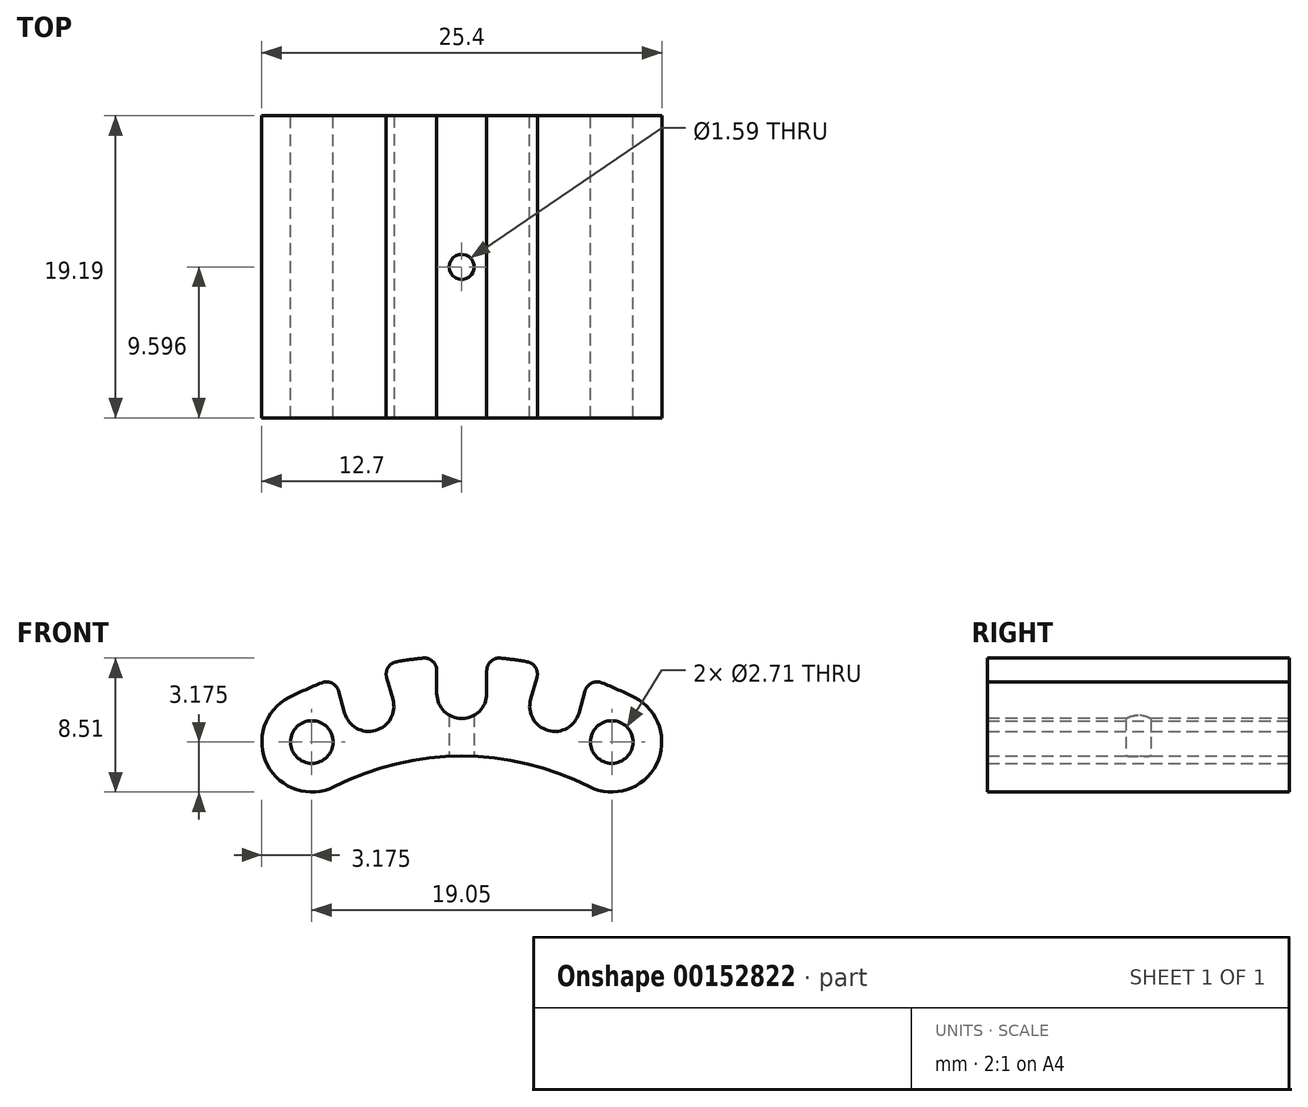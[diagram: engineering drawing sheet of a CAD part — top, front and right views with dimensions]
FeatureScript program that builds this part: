
annotation { "Feature Type Name" : "Feature", "Feature Type Description" : "" }
export const myFeature = defineFeature(function(context is Context, id is Id, definition is map)
    precondition{}
    {
        {
            var Q0;
            Q0=qCreatedBy(makeId("Front.planeOp"),FACE);
            var sketch = newSketch(context, id + "F0", { "sketchPlane" : qUnion([Q0])});
            skLineSegment(sketch, "E0", {"start": v(0, 0) * mm, "end": v(0, 17.86) * mm, "construction": true});
            skArc(sketch, "E1", {"start": v(8.09, 15.92) * mm, "mid": v(0, 17.86) * mm, "end": v(-8.09, 15.92) * mm});
            skLineSegment(sketch, "E2", {"start": v(-8.09, 15.92) * mm, "end": v(0, 0) * mm, "construction": true});
            skLineSegment(sketch, "E3", {"start": v(0, 0) * mm, "end": v(8.09, 15.92) * mm, "construction": true});
            skArc(sketch, "E4", {"start": v(-10.96, 21.59) * mm, "mid": v(-12.36, 17.32) * mm, "end": v(-8.09, 15.92) * mm});
            skArc(sketch, "E5", {"start": v(8.09, 15.92) * mm, "mid": v(12.36, 17.32) * mm, "end": v(10.96, 21.59) * mm});
            skArc(sketch, "E6", {"start": v(10.96, 21.59) * mm, "mid": v(0, 24.2) * mm, "end": v(-10.96, 21.59) * mm});
            skCircle(sketch, "E7", {"center": v(-9.53, 18.75) * mm, "radius": 1.35 * mm});
            skCircle(sketch, "E8", {"center": v(9.53, 18.75) * mm, "radius": 1.35 * mm});
            skSolve(sketch);
        }
        {
            var Q0;
            Q0 = qSketchRegion(id + "F0", true);
            extrude(context, id + "F1", {"entities" : qUnion([Q0]), "depth" : 19.2 * mm});
        }
        {
            var Q0;
            Q0=makeQuery(id+"F1.opExtrude","CAP_FACE",FACE,{"disambiguationData":[OSD([sQuery(id+"F0.wireOp",EDGE,"E1"),sQuery(id+"F0.wireOp",EDGE,"E4"),sQuery(id+"F0.wireOp",EDGE,"E5"),sQuery(id+"F0.wireOp",EDGE,"E6"),sQuery(id+"F0.wireOp",EDGE,"E7"),sQuery(id+"F0.wireOp",EDGE,"E8")])],"isStart":false});
            var sketch = newSketch(context, id + "F2", { "sketchPlane" : qUnion([Q0])});
            skLineSegment(sketch, "E9", {"start": v(0, 0) * mm, "end": v(-4.83, 17.2) * mm, "construction": true});
            skLineSegment(sketch, "E10", {"start": v(-4.83, 17.2) * mm, "end": v(-5.47, 19.49) * mm, "construction": true});
            skLineSegment(sketch, "E11.bottom", {"start": v(-7, 19.06) * mm, "end": v(-3.95, 19.92) * mm});
            skLineSegment(sketch, "E11.top", {"start": v(-8.08, 22.88) * mm, "end": v(-5.02, 23.74) * mm});
            skLineSegment(sketch, "E11.left", {"start": v(-7, 19.06) * mm, "end": v(-8.08, 22.88) * mm});
            skLineSegment(sketch, "E11.right", {"start": v(-3.95, 19.92) * mm, "end": v(-5.02, 23.74) * mm});
            skLineSegment(sketch, "E12", {"start": v(0, 0) * mm, "end": v(4.83, 17.2) * mm, "construction": true});
            skLineSegment(sketch, "E13", {"start": v(4.83, 17.2) * mm, "end": v(5.47, 19.49) * mm, "construction": true});
            skLineSegment(sketch, "E14.bottom", {"start": v(5.02, 23.74) * mm, "end": v(8.08, 22.88) * mm});
            skLineSegment(sketch, "E14.top", {"start": v(3.95, 19.92) * mm, "end": v(7, 19.06) * mm});
            skLineSegment(sketch, "E14.left", {"start": v(5.02, 23.74) * mm, "end": v(3.95, 19.92) * mm});
            skLineSegment(sketch, "E14.right", {"start": v(8.08, 22.88) * mm, "end": v(7, 19.06) * mm});
            skLineSegment(sketch, "E15", {"start": v(0, 0) * mm, "end": v(0, 17.86) * mm, "construction": true});
            skLineSegment(sketch, "E16", {"start": v(0, 17.86) * mm, "end": v(0, 20.24) * mm, "construction": true});
            skLineSegment(sketch, "E17.bottom", {"start": v(-1.59, 20.24) * mm, "end": v(1.59, 20.24) * mm});
            skLineSegment(sketch, "E17.top", {"start": v(-1.59, 24.2) * mm, "end": v(1.59, 24.2) * mm});
            skLineSegment(sketch, "E17.left", {"start": v(-1.59, 20.24) * mm, "end": v(-1.59, 24.2) * mm});
            skLineSegment(sketch, "E17.right", {"start": v(1.59, 20.24) * mm, "end": v(1.59, 24.2) * mm});
            skLineSegment(sketch, "E18", {"start": v(-3.95, 19.92) * mm, "end": v(-1.59, 20.24) * mm, "construction": true});
            skLineSegment(sketch, "E19", {"start": v(1.59, 20.24) * mm, "end": v(3.95, 19.92) * mm, "construction": true});
            skSolve(sketch);
        }
        {
            var Q0;
            Q0 = qSketchRegion(id + "F2", true);
            var Q1;
            Q1=makeQuery(id+"F1.opExtrude","CAP_FACE",FACE,{"disambiguationData":[OSD([sQuery(id+"F0.wireOp",EDGE,"E1"),sQuery(id+"F0.wireOp",EDGE,"E4"),sQuery(id+"F0.wireOp",EDGE,"E5"),sQuery(id+"F0.wireOp",EDGE,"E6"),sQuery(id+"F0.wireOp",EDGE,"E7"),sQuery(id+"F0.wireOp",EDGE,"E8")])],"isStart":true});
            extrude(context, id + "F3", {"entities" : qUnion([Q0]), "operationType" : NewBodyOperationType.REMOVE, "endBound" : BoundingType.UP_TO_SURFACE, "oppositeDirection" : true, "endBoundEntityFace" : qUnion([Q1]), "depth" : 25.4 * mm});
        }
        {
            var Q0;
            Q0=makeQuery(id+"F3.boolean.opBoolean","COPY",EDGE,{"derivedFrom":makeQuery(id+"F3.opExtrude","SWEPT_EDGE",EDGE,{"disambiguationData":[OSD([sQuery(id+"F2.wireOp",EDGE,"E11.bottom"),sQuery(id+"F2.wireOp",EDGE,"E11.left")])]})});
            var Q1;
            Q1=makeQuery(id+"F3.boolean.opBoolean","COPY",EDGE,{"derivedFrom":makeQuery(id+"F3.opExtrude","SWEPT_EDGE",EDGE,{"disambiguationData":[OSD([sQuery(id+"F2.wireOp",EDGE,"E11.bottom"),sQuery(id+"F2.wireOp",EDGE,"E11.right")])]})});
            var Q2;
            Q2=makeQuery(id+"F3.boolean.opBoolean","COPY",EDGE,{"derivedFrom":makeQuery(id+"F3.opExtrude","SWEPT_EDGE",EDGE,{"disambiguationData":[OSD([sQuery(id+"F2.wireOp",EDGE,"E17.bottom"),sQuery(id+"F2.wireOp",EDGE,"E17.left")])]})});
            var Q3;
            Q3=makeQuery(id+"F3.boolean.opBoolean","COPY",EDGE,{"derivedFrom":makeQuery(id+"F3.opExtrude","SWEPT_EDGE",EDGE,{"disambiguationData":[OSD([sQuery(id+"F2.wireOp",EDGE,"E17.bottom"),sQuery(id+"F2.wireOp",EDGE,"E17.right")])]})});
            var Q4;
            Q4=makeQuery(id+"F3.boolean.opBoolean","COPY",EDGE,{"derivedFrom":makeQuery(id+"F3.opExtrude","SWEPT_EDGE",EDGE,{"disambiguationData":[OSD([sQuery(id+"F2.wireOp",EDGE,"E14.top"),sQuery(id+"F2.wireOp",EDGE,"E14.left")])]})});
            var Q5;
            Q5=makeQuery(id+"F3.boolean.opBoolean","COPY",EDGE,{"derivedFrom":makeQuery(id+"F3.opExtrude","SWEPT_EDGE",EDGE,{"disambiguationData":[OSD([sQuery(id+"F2.wireOp",EDGE,"E14.top"),sQuery(id+"F2.wireOp",EDGE,"E14.right")])]})});
            fillet(context, id + "F4", {"entities" : qUnion([Q0, Q1, Q2, Q3, Q4, Q5]), "radius" : 1.59 * mm, "tangentPropagation" : true, "allowEdgeOverflow" : false});
        }
        {
            var Q0;
            Q0=makeQuery(id+"F3.boolean.opBoolean","INTERSECT",EDGE,{"derivedFrom":[makeQuery(id+"F1.opExtrude","SWEPT_FACE",FACE,{"disambiguationData":[OSD([sQuery(id+"F0.wireOp",EDGE,"E6")])]}),makeQuery(id+"F3.opExtrude","SWEPT_FACE",FACE,{"disambiguationData":[OSD([sQuery(id+"F2.wireOp",EDGE,"E11.left")])]})]});
            var Q1;
            Q1=makeQuery(id+"F3.boolean.opBoolean","INTERSECT",EDGE,{"derivedFrom":[makeQuery(id+"F1.opExtrude","SWEPT_FACE",FACE,{"disambiguationData":[OSD([sQuery(id+"F0.wireOp",EDGE,"E6")])]}),makeQuery(id+"F3.opExtrude","SWEPT_FACE",FACE,{"disambiguationData":[OSD([sQuery(id+"F2.wireOp",EDGE,"E11.right")])]})]});
            var Q2;
            Q2=makeQuery(id+"F3.boolean.opBoolean","INTERSECT",EDGE,{"derivedFrom":[makeQuery(id+"F1.opExtrude","SWEPT_FACE",FACE,{"disambiguationData":[OSD([sQuery(id+"F0.wireOp",EDGE,"E6")])]}),makeQuery(id+"F3.opExtrude","SWEPT_FACE",FACE,{"disambiguationData":[OSD([sQuery(id+"F2.wireOp",EDGE,"E17.left")])]})]});
            var Q3;
            Q3=makeQuery(id+"F3.boolean.opBoolean","INTERSECT",EDGE,{"derivedFrom":[makeQuery(id+"F1.opExtrude","SWEPT_FACE",FACE,{"disambiguationData":[OSD([sQuery(id+"F0.wireOp",EDGE,"E6")])]}),makeQuery(id+"F3.opExtrude","SWEPT_FACE",FACE,{"disambiguationData":[OSD([sQuery(id+"F2.wireOp",EDGE,"E17.right")])]})]});
            var Q4;
            Q4=makeQuery(id+"F3.boolean.opBoolean","INTERSECT",EDGE,{"derivedFrom":[makeQuery(id+"F1.opExtrude","SWEPT_FACE",FACE,{"disambiguationData":[OSD([sQuery(id+"F0.wireOp",EDGE,"E6")])]}),makeQuery(id+"F3.opExtrude","SWEPT_FACE",FACE,{"disambiguationData":[OSD([sQuery(id+"F2.wireOp",EDGE,"E14.left")])]})]});
            var Q5;
            Q5=makeQuery(id+"F3.boolean.opBoolean","INTERSECT",EDGE,{"derivedFrom":[makeQuery(id+"F1.opExtrude","SWEPT_FACE",FACE,{"disambiguationData":[OSD([sQuery(id+"F0.wireOp",EDGE,"E6")])]}),makeQuery(id+"F3.opExtrude","SWEPT_FACE",FACE,{"disambiguationData":[OSD([sQuery(id+"F2.wireOp",EDGE,"E14.right")])]})]});
            fillet(context, id + "F5", {"entities" : qUnion([Q0, Q1, Q2, Q3, Q4, Q5]), "radius" : 0.8 * mm, "tangentPropagation" : true, "allowEdgeOverflow" : false});
        }
        {
            var Q0;
            Q0=qCreatedBy(makeId("Top.planeOp"),FACE);
            var sketch = newSketch(context, id + "F6", { "sketchPlane" : qUnion([Q0])});
            skLineSegment(sketch, "E20", {"start": v(0, 0) * mm, "end": v(0, -19.19) * mm, "construction": true});
            skCircle(sketch, "E21", {"center": v(0, -9.6) * mm, "radius": 0.8 * mm});
            skSolve(sketch);
        }
        {
            var Q0;
            Q0 = qSketchRegion(id + "F6", true);
            var Q1;
            {var subQ2=sQuery(id+"F0.wireOp",EDGE,"E6");Q1=makeQuery(id+"F3.boolean.opBoolean","SPLIT",FACE,{"disambiguationData":[TD([makeQuery(id+"F3.opExtrude","SWEPT_FACE",FACE,{"disambiguationData":[OSD([sQuery(id+"F2.wireOp",EDGE,"E14.left")])]})])],"derivedFrom":makeQuery(id+"F1.opExtrude","SWEPT_FACE",FACE,{"disambiguationData":[OSD([subQ2])]})});}
            extrude(context, id + "F7", {"entities" : qUnion([Q0]), "operationType" : NewBodyOperationType.REMOVE, "endBound" : BoundingType.UP_TO_SURFACE, "endBoundEntityFace" : qUnion([Q1]), "depth" : 25.4 * mm});
        }
    });
